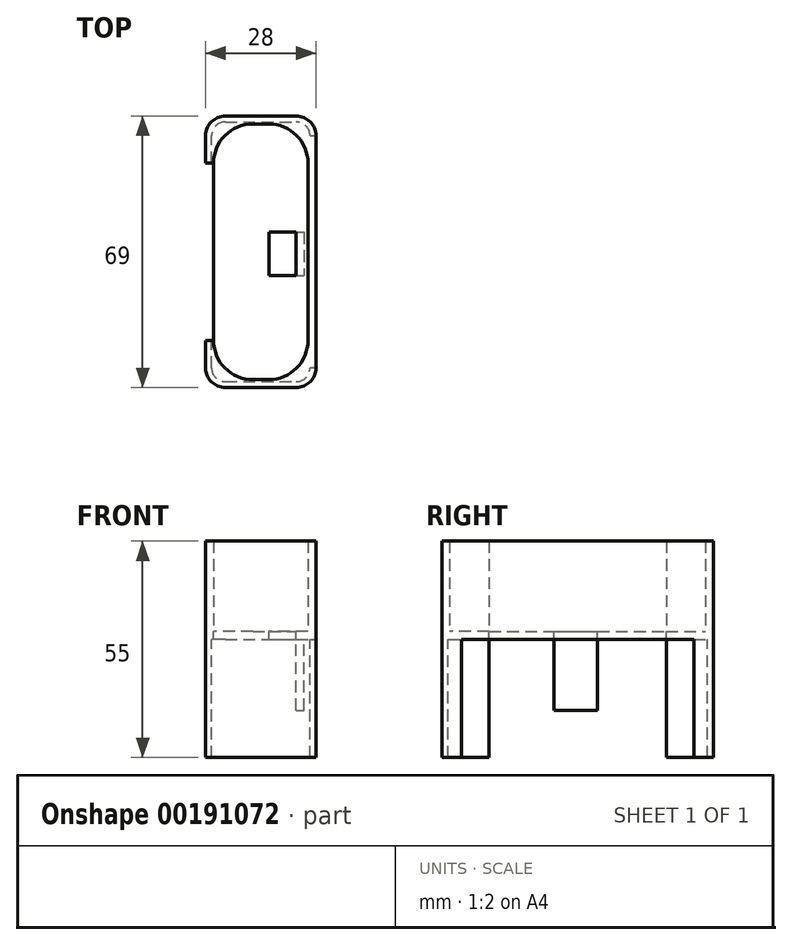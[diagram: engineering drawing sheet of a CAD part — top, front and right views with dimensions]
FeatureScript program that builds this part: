
annotation { "Feature Type Name" : "Feature", "Feature Type Description" : "" }
export const myFeature = defineFeature(function(context is Context, id is Id, definition is map)
    precondition{}
    {
        {
            var Q0;
            Q0=qCreatedBy(makeId("Top.planeOp"),FACE);
            var sketch = newSketch(context, id + "F0", { "sketchPlane" : qUnion([Q0])});
            skLineSegment(sketch, "E0.bottom", {"start": v(-28.13, -31.2) * mm, "end": v(-0.13, -31.2) * mm});
            skLineSegment(sketch, "E0.top", {"start": v(-28.13, 37.8) * mm, "end": v(-0.13, 37.8) * mm});
            skLineSegment(sketch, "E0.left", {"start": v(-28.13, -31.2) * mm, "end": v(-28.13, 37.8) * mm});
            skLineSegment(sketch, "E0.right", {"start": v(-0.13, -31.2) * mm, "end": v(-0.13, 37.8) * mm});
            skSolve(sketch);
        }
        {
            var Q0;
            Q0 = qSketchRegion(id + "F0", true);
            extrude(context, id + "F1", {"entities" : qUnion([Q0]), "depth" : 25 * mm});
        }
        {
            var Q0;
            Q0=makeQuery(id+"F1.opExtrude","CAP_FACE",FACE,{"disambiguationData":[OSD([sQuery(id+"F0.wireOp",EDGE,"E0.bottom"),sQuery(id+"F0.wireOp",EDGE,"E0.top"),sQuery(id+"F0.wireOp",EDGE,"E0.left"),sQuery(id+"F0.wireOp",EDGE,"E0.right")])],"isStart":false});
            shell(context, id + "F2", {"entities" : qUnion([Q0]), "thickness" : 2 * mm});
        }
        {
            var Q0;
            Q0=makeQuery(id+"F1.opExtrude","SWEPT_EDGE",EDGE,{"disambiguationData":[OSD([sQuery(id+"F0.wireOp",EDGE,"E0.bottom"),sQuery(id+"F0.wireOp",EDGE,"E0.right")])]});
            var Q1;
            Q1=makeQuery(id+"F1.opExtrude","SWEPT_EDGE",EDGE,{"disambiguationData":[OSD([sQuery(id+"F0.wireOp",EDGE,"E0.bottom"),sQuery(id+"F0.wireOp",EDGE,"E0.left")])]});
            var Q2;
            Q2=makeQuery(id+"F1.opExtrude","SWEPT_EDGE",EDGE,{"disambiguationData":[OSD([sQuery(id+"F0.wireOp",EDGE,"E0.top"),sQuery(id+"F0.wireOp",EDGE,"E0.right")])]});
            var Q3;
            Q3=makeQuery(id+"F1.opExtrude","SWEPT_EDGE",EDGE,{"disambiguationData":[OSD([sQuery(id+"F0.wireOp",EDGE,"E0.top"),sQuery(id+"F0.wireOp",EDGE,"E0.left")])]});
            fillet(context, id + "F3", {"entities" : qUnion([Q0, Q1, Q2, Q3]), "radius" : 5 * mm, "tangentPropagation" : true, "allowEdgeOverflow" : false});
        }
        {
            var Q0;
            Q0=makeQuery(id+"F2.opShell","OFFSET_EDGE",EDGE,{"disambiguationData":[OSD([sQuery(id+"F0.wireOp",EDGE,"E0.top"),sQuery(id+"F0.wireOp",EDGE,"E0.left")])]});
            var Q1;
            Q1=makeQuery(id+"F2.opShell","OFFSET_EDGE",EDGE,{"disambiguationData":[OSD([sQuery(id+"F0.wireOp",EDGE,"E0.bottom"),sQuery(id+"F0.wireOp",EDGE,"E0.left")])]});
            var Q2;
            Q2=makeQuery(id+"F2.opShell","OFFSET_EDGE",EDGE,{"disambiguationData":[OSD([sQuery(id+"F0.wireOp",EDGE,"E0.bottom"),sQuery(id+"F0.wireOp",EDGE,"E0.right")])]});
            var Q3;
            Q3=makeQuery(id+"F2.opShell","OFFSET_EDGE",EDGE,{"disambiguationData":[OSD([sQuery(id+"F0.wireOp",EDGE,"E0.top"),sQuery(id+"F0.wireOp",EDGE,"E0.right")])]});
            fillet(context, id + "F4", {"entities" : qUnion([Q0, Q1, Q2, Q3]), "radius" : 10 * mm, "tangentPropagation" : true, "allowEdgeOverflow" : false});
        }
        {
            var Q0;
            Q0=makeQuery(id+"F2.opShell","OFFSET_FACE",FACE,{"disambiguationData":[OSD([sQuery(id+"F0.wireOp",EDGE,"E0.bottom"),sQuery(id+"F0.wireOp",EDGE,"E0.top"),sQuery(id+"F0.wireOp",EDGE,"E0.left"),sQuery(id+"F0.wireOp",EDGE,"E0.right")])]});
            var sketch = newSketch(context, id + "F5", { "sketchPlane" : qUnion([Q0])});
            skLineSegment(sketch, "E1.bottom", {"start": v(-12.03, -2.7) * mm, "end": v(-5.13, -2.7) * mm});
            skLineSegment(sketch, "E1.top", {"start": v(-12.03, 8.3) * mm, "end": v(-5.13, 8.3) * mm});
            skLineSegment(sketch, "E1.left", {"start": v(-12.03, -2.7) * mm, "end": v(-12.03, 8.3) * mm});
            skLineSegment(sketch, "E1.right", {"start": v(-5.13, -2.7) * mm, "end": v(-5.13, 8.3) * mm});
            skSolve(sketch);
        }
        {
            var Q0;
            Q0=makeQuery(id+"F5.imprint","IMPRINT",FACE,{"disambiguationData":[TD([[makeQuery(id+"F5.imprint","IMPRINT",EDGE,{"derivedFrom":sQuery(id+"F5.wireOp",EDGE,"E1.bottom")}),1.0]])]});
            extrude(context, id + "F6", {"entities" : qUnion([Q0]), "operationType" : NewBodyOperationType.REMOVE, "oppositeDirection" : true, "depth" : 25 * mm});
        }
        {
            var Q0;
            Q0=makeQuery(id+"F1.opExtrude","CAP_FACE",FACE,{"disambiguationData":[OSD([sQuery(id+"F0.wireOp",EDGE,"E0.bottom"),sQuery(id+"F0.wireOp",EDGE,"E0.top"),sQuery(id+"F0.wireOp",EDGE,"E0.left"),sQuery(id+"F0.wireOp",EDGE,"E0.right")])],"isStart":false});
            var sketch = newSketch(context, id + "F7", { "sketchPlane" : qUnion([Q0])});
            skLineSegment(sketch, "E2.bottom", {"start": v(-26.13, 25.8) * mm, "end": v(-28.13, 25.8) * mm});
            skLineSegment(sketch, "E2.top", {"start": v(-26.13, -19.2) * mm, "end": v(-28.13, -19.2) * mm});
            skLineSegment(sketch, "E2.left", {"start": v(-26.13, 25.8) * mm, "end": v(-26.13, -19.2) * mm});
            skLineSegment(sketch, "E2.right", {"start": v(-28.13, 25.8) * mm, "end": v(-28.13, -19.2) * mm});
            skSolve(sketch);
        }
        {
            var Q0;
            Q0 = qSketchRegion(id + "F7", true);
            extrude(context, id + "F8", {"entities" : qUnion([Q0]), "operationType" : NewBodyOperationType.REMOVE, "oppositeDirection" : true, "depth" : 25 * mm});
        }
        {
            var Q0;
            Q0=makeQuery(id+"F1.opExtrude","CAP_FACE",FACE,{"disambiguationData":[OSD([sQuery(id+"F0.wireOp",EDGE,"E0.bottom"),sQuery(id+"F0.wireOp",EDGE,"E0.top"),sQuery(id+"F0.wireOp",EDGE,"E0.left"),sQuery(id+"F0.wireOp",EDGE,"E0.right")])],"isStart":true});
            var sketch = newSketch(context, id + "F9", { "sketchPlane" : qUnion([Q0])});
            skSolve(sketch);
        }
        {
            var Q0;
            {var subQ3=sQuery(id+"F0.wireOp",EDGE,"E0.bottom");Q0=makeQuery(id+"F9.imprint","IMPRINT",FACE,{"disambiguationData":[TD([[makeQuery(id+"F9.imprint","IMPRINT",EDGE,{"derivedFrom":makeQuery(id+"F1.opExtrude","CAP_EDGE",EDGE,{"disambiguationData":[OSD([subQ3])],"isStart":true})}),-1.0]])]});}
            var sketch = newSketch(context, id + "F10", { "sketchPlane" : qUnion([Q0])});
            skLineSegment(sketch, "E3.0", {"start": v(-5.13, 2.7) * mm, "end": v(-5.13, -8.3) * mm});
            skLineSegment(sketch, "E4.bottom", {"start": v(-5.13, -8.3) * mm, "end": v(-3.13, -8.3) * mm});
            skLineSegment(sketch, "E4.top", {"start": v(-5.13, 2.7) * mm, "end": v(-3.13, 2.7) * mm});
            skLineSegment(sketch, "E4.left", {"start": v(-5.13, -8.3) * mm, "end": v(-5.13, 2.7) * mm});
            skLineSegment(sketch, "E4.right", {"start": v(-3.13, -8.3) * mm, "end": v(-3.13, 2.7) * mm});
            skArc(sketch, "E5.0", {"start": v(-5.13, -36.3) * mm, "mid": v(-2.66, -35.27) * mm, "end": v(-1.63, -32.8) * mm});
            skLineSegment(sketch, "E5.1", {"start": v(-23.13, -36.3) * mm, "end": v(-5.13, -36.3) * mm});
            skArc(sketch, "E5.2", {"start": v(-26.63, -32.8) * mm, "mid": v(-25.6, -35.27) * mm, "end": v(-23.13, -36.3) * mm});
            skLineSegment(sketch, "E5.3", {"start": v(-26.63, -25.8) * mm, "end": v(-26.63, -32.8) * mm});
            skLineSegment(sketch, "E6.0", {"start": v(-26.63, 26.2) * mm, "end": v(-26.63, 19.2) * mm});
            skArc(sketch, "E6.1", {"start": v(-23.13, 29.7) * mm, "mid": v(-25.6, 28.68) * mm, "end": v(-26.63, 26.2) * mm});
            skLineSegment(sketch, "E6.2", {"start": v(-23.13, 29.7) * mm, "end": v(-5.13, 29.7) * mm});
            skArc(sketch, "E6.3", {"start": v(-1.63, 26.2) * mm, "mid": v(-2.66, 28.68) * mm, "end": v(-5.13, 29.7) * mm});
            skLineSegment(sketch, "E7", {"start": v(-1.63, -32.8) * mm, "end": v(-0.13, -32.8) * mm});
            skLineSegment(sketch, "E8.0", {"start": v(-0.13, 26.2) * mm, "end": v(-0.13, -32.8) * mm});
            skLineSegment(sketch, "E9", {"start": v(-0.13, 26.2) * mm, "end": v(-1.63, 26.2) * mm});
            skLineSegment(sketch, "E10.0", {"start": v(-26.13, 19.2) * mm, "end": v(-28.13, 19.2) * mm});
            skLineSegment(sketch, "E11.0", {"start": v(-26.13, -25.8) * mm, "end": v(-28.13, -25.8) * mm});
            skSolve(sketch);
        }
        {
            var Q0;
            Q0=makeQuery(id+"F10.imprint","IMPRINT",FACE,{"disambiguationData":[TD([[makeQuery(id+"F10.imprint","IMPRINT",EDGE,{"derivedFrom":sQuery(id+"F10.wireOp",EDGE,"E4.bottom")}),1.0]])]});
            extrude(context, id + "F11", {"entities" : qUnion([Q0]), "operationType" : NewBodyOperationType.ADD, "depth" : 18 * mm});
        }
        {
            var Q0;
            Q0=makeQuery(id+"F10.imprint","IMPRINT",FACE,{"disambiguationData":[TD([[makeQuery(id+"F10.imprint","IMPRINT",EDGE,{"derivedFrom":sQuery(id+"F10.wireOp",EDGE,"E5.0")}),-1.0]])]});
            var Q1;
            {var subQ1=sQuery(id+"F10.wireOp",EDGE,"E6.0");Q1=makeQuery(id+"F10.imprint","IMPRINT",FACE,{"disambiguationData":[TD([[makeQuery(id+"F10.imprint","IMPRINT",EDGE,{"derivedFrom":subQ1}),-1.0]])]});}
            extrude(context, id + "F12", {"entities" : qUnion([Q0, Q1]), "operationType" : NewBodyOperationType.ADD, "depth" : 30 * mm});
        }
    });
